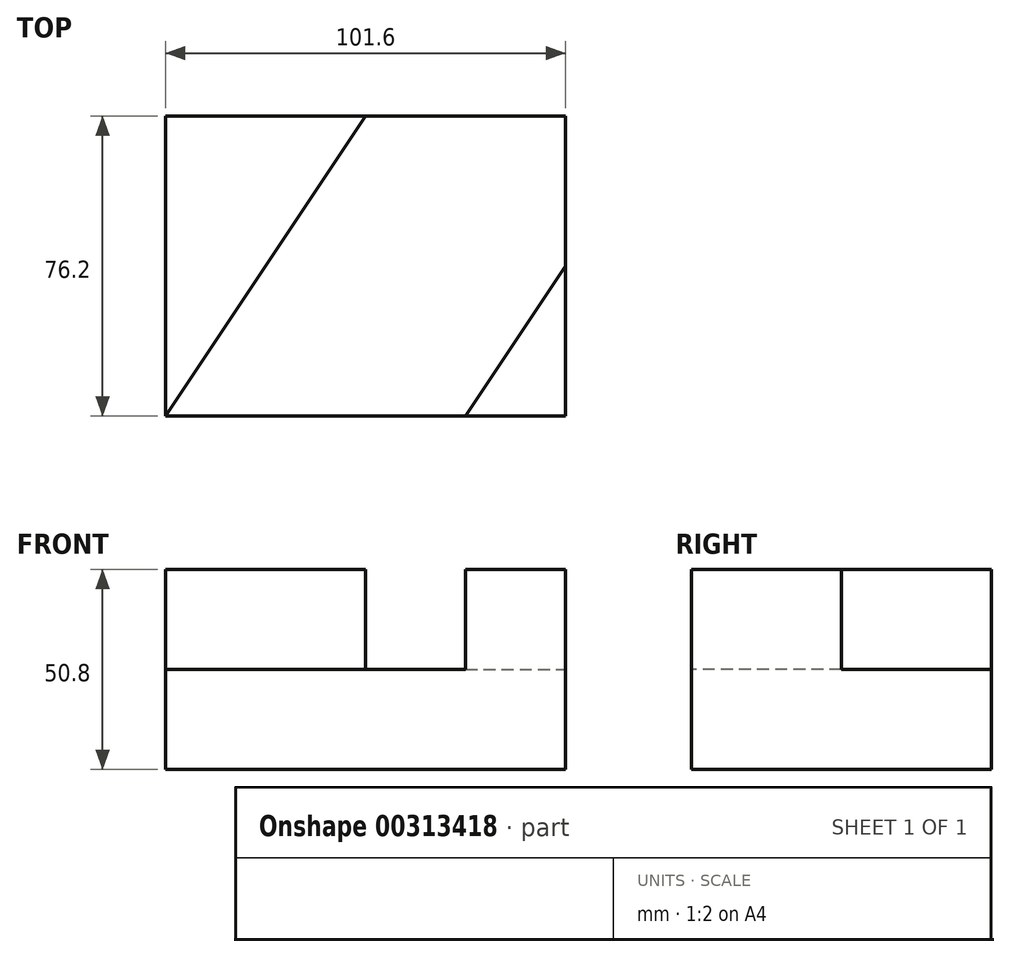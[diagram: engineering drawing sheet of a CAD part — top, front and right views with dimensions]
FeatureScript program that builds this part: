
annotation { "Feature Type Name" : "Feature", "Feature Type Description" : "" }
export const myFeature = defineFeature(function(context is Context, id is Id, definition is map)
    precondition{}
    {
        {
            var Q0;
            Q0=qCreatedBy(makeId("Front.planeOp"),FACE);
            var sketch = newSketch(context, id + "F0", { "sketchPlane" : qUnion([Q0])});
            skLineSegment(sketch, "E0", {"start": v(-38.53, -48.63) * mm, "end": v(63.07, -48.63) * mm});
            skLineSegment(sketch, "E1", {"start": v(-38.53, -48.63) * mm, "end": v(-38.53, -23.23) * mm});
            skLineSegment(sketch, "E2", {"start": v(-38.53, -23.23) * mm, "end": v(63.07, -23.23) * mm});
            skLineSegment(sketch, "E3", {"start": v(63.07, -23.23) * mm, "end": v(63.07, -48.63) * mm});
            skSolve(sketch);
        }
        {
            var Q0;
            Q0=makeQuery(id+"F0.imprint","IMPRINT",FACE,{"disambiguationData":[TD([[makeQuery(id+"F0.imprint","IMPRINT",EDGE,{"derivedFrom":sQuery(id+"F0.wireOp",EDGE,"E0")}),1.0]])]});
            extrude(context, id + "F1", {"entities" : qUnion([Q0]), "depth" : 76.2 * mm});
        }
        {
            var Q0;
            Q0=makeQuery(id+"F1.opExtrude","SWEPT_FACE",FACE,{"disambiguationData":[OSD([sQuery(id+"F0.wireOp",EDGE,"E2")])]});
            var sketch = newSketch(context, id + "F2", { "sketchPlane" : qUnion([Q0])});
            skLineSegment(sketch, "E4", {"start": v(63.07, -76.2) * mm, "end": v(63.07, -38.1) * mm});
            skLineSegment(sketch, "E5", {"start": v(63.07, -76.2) * mm, "end": v(37.67, -76.2) * mm});
            skLineSegment(sketch, "E6", {"start": v(37.67, -76.2) * mm, "end": v(63.07, -38.1) * mm});
            skLineSegment(sketch, "E7", {"start": v(-38.53, -76.2) * mm, "end": v(-38.53, 0) * mm});
            skLineSegment(sketch, "E8", {"start": v(-38.53, 0) * mm, "end": v(12.27, 0) * mm});
            skLineSegment(sketch, "E9", {"start": v(12.27, 0) * mm, "end": v(-38.53, -76.2) * mm});
            skSolve(sketch);
        }
        {
            var Q0;
            Q0=makeQuery(id+"F2.imprint","IMPRINT",FACE,{"disambiguationData":[TD([[makeQuery(id+"F2.imprint","IMPRINT",EDGE,{"derivedFrom":sQuery(id+"F2.wireOp",EDGE,"E4")}),1.0]])]});
            var Q1;
            Q1=makeQuery(id+"F2.imprint","IMPRINT",FACE,{"disambiguationData":[TD([[makeQuery(id+"F2.imprint","IMPRINT",EDGE,{"derivedFrom":sQuery(id+"F2.wireOp",EDGE,"E7")}),-1.0]])]});
            extrude(context, id + "F3", {"entities" : qUnion([Q0, Q1]), "operationType" : NewBodyOperationType.ADD, "depth" : 25.4 * mm});
        }
    });
